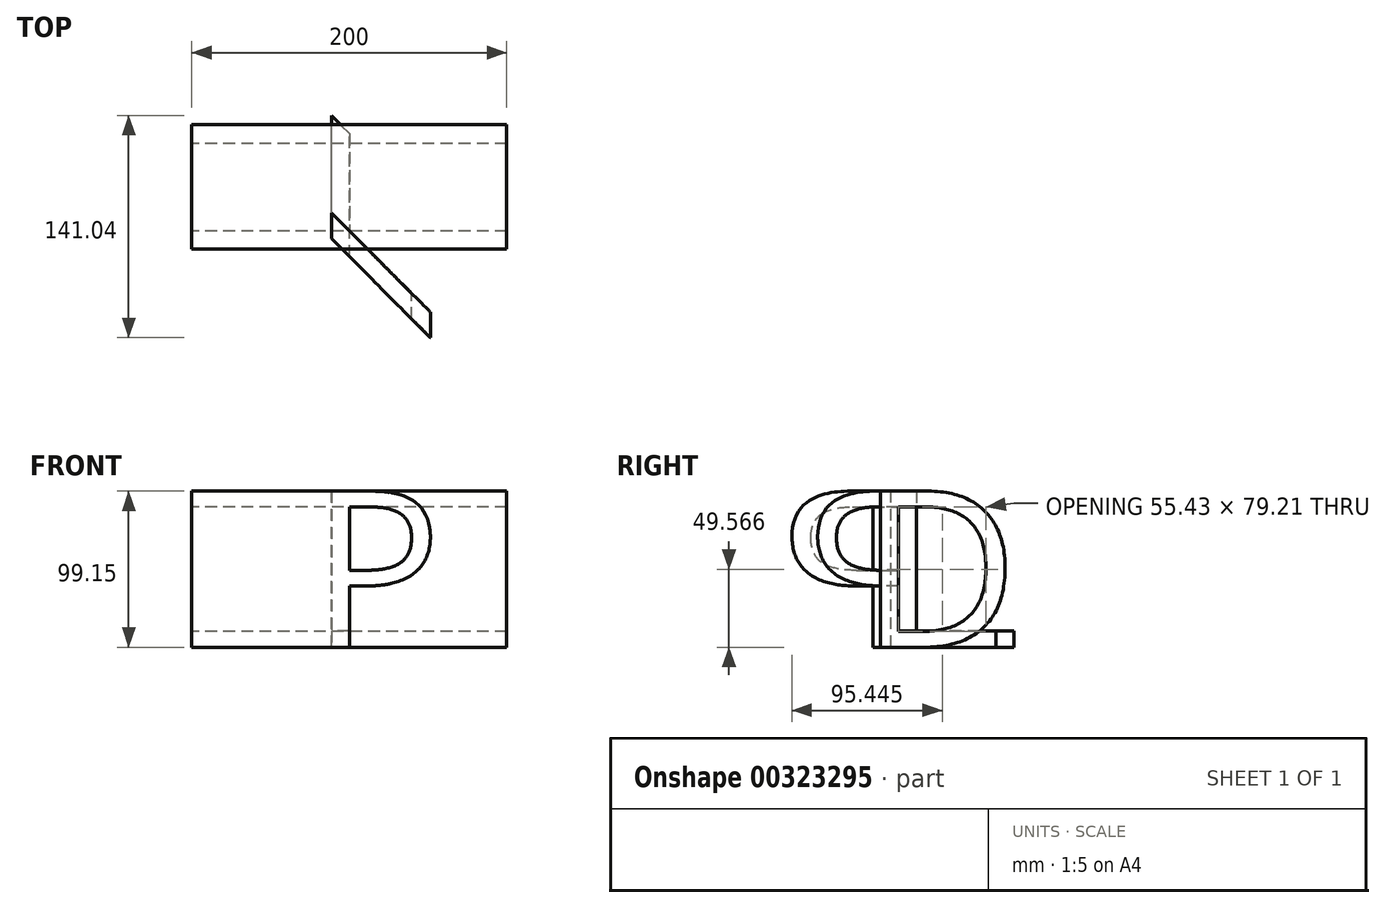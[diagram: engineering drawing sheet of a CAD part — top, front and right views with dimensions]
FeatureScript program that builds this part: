
annotation { "Feature Type Name" : "Feature", "Feature Type Description" : "" }
export const myFeature = defineFeature(function(context is Context, id is Id, definition is map)
    precondition{}
    {
        {
            var Q0;
            Q0=qCreatedBy(makeId("Top.planeOp"),FACE);
            var sketch = newSketch(context, id + "F0", { "sketchPlane" : qUnion([Q0])});
            skLineSegment(sketch, "E0", {"start": v(-48.7, -48.7) * mm, "end": v(74.45, 74.45) * mm, "construction": true});
            skSolve(sketch);
        }
        {
            var Q0;
            Q0=sQuery(id+"F0.wireOp",EDGE,"E0");
            cPlane(context, id + "F1", {"entities" : qUnion([Q0]), "cplaneType" : CPlaneType.LINE_ANGLE, "offset" : 25 * mm, "angle" : 90 * degree, "width" : 150 * mm, "height" : 150 * mm});
        }
        {
            var Q0;
            Q0=qCreatedBy(makeId("Front.planeOp"),FACE);
            var sketch = newSketch(context, id + "F2", { "sketchPlane" : qUnion([Q0])});
            skLineSegment(sketch, "E1.bottom", {"start": v(-25, 50) * mm, "end": v(25, 50) * mm, "construction": true});
            skLineSegment(sketch, "E1.top", {"start": v(-25, -50) * mm, "end": v(25, -50) * mm, "construction": true});
            skLineSegment(sketch, "E1.left", {"start": v(-25, 50) * mm, "end": v(-25, -50) * mm, "construction": true});
            skLineSegment(sketch, "E1.right", {"start": v(25, 50) * mm, "end": v(25, -50) * mm, "construction": true});
            skPoint(sketch, "E1.middle", {"position": v(0, 0) * mm});
            skText(sketch, "E2", { "text": "P", "fontName": "OpenSans-Regular.ttf"});
            const initialGuessF2  = {"E2": [-0.025, -0.05, 1, 0, 0.1]};
            skSetInitialGuess(sketch, initialGuessF2);
            skSolve(sketch);
        }
        {
            var Q0;
            Q0=qCreatedBy(id+"F1.planeOp",FACE);
            var sketch = newSketch(context, id + "F3", { "sketchPlane" : qUnion([Q0])});
            skLineSegment(sketch, "E3.bottom", {"start": v(25, 50) * mm, "end": v(-25, 50) * mm, "construction": true});
            skLineSegment(sketch, "E3.top", {"start": v(25, -50) * mm, "end": v(-25, -50) * mm, "construction": true});
            skLineSegment(sketch, "E3.left", {"start": v(25, 50) * mm, "end": v(25, -50) * mm, "construction": true});
            skLineSegment(sketch, "E3.right", {"start": v(-25, 50) * mm, "end": v(-25, -50) * mm, "construction": true});
            skPoint(sketch, "E3.middle", {"position": v(0, 0) * mm});
            skText(sketch, "E4", { "text": "L", "fontName": "OpenSans-Regular.ttf"});
            const initialGuessF3  = {"E4": [-0.025, -0.05, 1, 0, 0.1]};
            skSetInitialGuess(sketch, initialGuessF3);
            skSolve(sketch);
        }
        {
            var Q0;
            Q0=qCreatedBy(makeId("Right.planeOp"),FACE);
            var sketch = newSketch(context, id + "F4", { "sketchPlane" : qUnion([Q0])});
            skLineSegment(sketch, "E5.bottom", {"start": v(-25, 50) * mm, "end": v(25, 50) * mm, "construction": true});
            skLineSegment(sketch, "E5.top", {"start": v(-25, -50) * mm, "end": v(25, -50) * mm, "construction": true});
            skLineSegment(sketch, "E5.left", {"start": v(-25, 50) * mm, "end": v(-25, -50) * mm, "construction": true});
            skLineSegment(sketch, "E5.right", {"start": v(25, 50) * mm, "end": v(25, -50) * mm, "construction": true});
            skPoint(sketch, "E5.middle", {"position": v(0, 0) * mm});
            skText(sketch, "E6", { "text": "D", "fontName": "OpenSans-Regular.ttf"});
            const initialGuessF4  = {"E6": [-0.025, -0.05, 1, 0, 0.1]};
            skSetInitialGuess(sketch, initialGuessF4);
            skSolve(sketch);
        }
        {
            var Q0;
            Q0 = qSketchRegion(id + "F2", true);
            extrude(context, id + "F5", {"entities" : qUnion([Q0]), "endBound" : BoundingType.SYMMETRIC, "depth" : 200 * mm});
        }
        {
            var Q0;
            Q0 = qSketchRegion(id + "F3", true);
            extrude(context, id + "F6", {"entities" : qUnion([Q0]), "endBound" : BoundingType.SYMMETRIC, "depth" : 200 * mm});
        }
        {
            var Q0;
            Q0 = qSketchRegion(id + "F4", true);
            extrude(context, id + "F7", {"entities" : qUnion([Q0]), "endBound" : BoundingType.SYMMETRIC, "depth" : 200 * mm});
        }
        {
            var Q0;
            Q0=makeQuery(id+"F5.opExtrude","SWEPT_BODY",BODY,{"disambiguationData":[OSD([sQuery(id+"F2.wireOp",EDGE,"E2.sketch_text.stroke-0"),sQuery(id+"F2.wireOp",EDGE,"E2.sketch_text.stroke-1"),sQuery(id+"F2.wireOp",EDGE,"E2.sketch_text.stroke-2"),sQuery(id+"F2.wireOp",EDGE,"E2.sketch_text.stroke-3"),sQuery(id+"F2.wireOp",EDGE,"E2.sketch_text.stroke-4"),sQuery(id+"F2.wireOp",EDGE,"E2.sketch_text.stroke-5"),sQuery(id+"F2.wireOp",EDGE,"E2.sketch_text.stroke-6"),sQuery(id+"F2.wireOp",EDGE,"E2.sketch_text.stroke-7"),sQuery(id+"F2.wireOp",EDGE,"E2.sketch_text.stroke-8"),sQuery(id+"F2.wireOp",EDGE,"E2.sketch_text.stroke-9"),sQuery(id+"F2.wireOp",EDGE,"E2.sketch_text.stroke-10"),sQuery(id+"F2.wireOp",EDGE,"E2.sketch_text.stroke-11"),sQuery(id+"F2.wireOp",EDGE,"E2.sketch_text.stroke-12"),sQuery(id+"F2.wireOp",EDGE,"E2.sketch_text.stroke-13"),sQuery(id+"F2.wireOp",EDGE,"E2.sketch_text.stroke-14")])]});
            var Q1;
            Q1=makeQuery(id+"F6.opExtrude","SWEPT_BODY",BODY,{"disambiguationData":[OSD([sQuery(id+"F3.wireOp",EDGE,"E4.sketch_text.stroke-0"),sQuery(id+"F3.wireOp",EDGE,"E4.sketch_text.stroke-1"),sQuery(id+"F3.wireOp",EDGE,"E4.sketch_text.stroke-2"),sQuery(id+"F3.wireOp",EDGE,"E4.sketch_text.stroke-3"),sQuery(id+"F3.wireOp",EDGE,"E4.sketch_text.stroke-4"),sQuery(id+"F3.wireOp",EDGE,"E4.sketch_text.stroke-5")])]});
            booleanBodies(context, id + "F8", {"operationType" : BooleanOperationType.INTERSECTION, "tools" : qUnion([Q0, Q1])});
        }
    });
